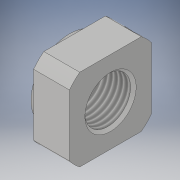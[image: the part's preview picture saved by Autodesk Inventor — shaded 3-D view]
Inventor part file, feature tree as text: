
AUTODESK INVENTOR PART (.ipt)
format: ipt  version: 2019 (Build 230136000, 136)  size: 162,304 bytes
history: native  units: mm
features: other x7, sketch x4, revolve x3, thread x2, extrude x1
ambient origin geometry x8: Origin, YZ Plane, XZ Plane, XY Plane, X Axis, Y Axis, Z Axis, Center Point
bodies: Solid1 (feature_tree)
feature tree (17):
  extrude  "Extrusion1"  TaperAngle=360.0deg  [1 undecoded]
  revolve  "Revolution1"  [1 undecoded]
  revolve  "Revolution2"  [1 undecoded]
  thread  "Thread1"  [1 undecoded]
  revolve  "Revolution3"  [1 undecoded]
  thread  "Thread2"  [1 undecoded]
  other  "to_collar_XY"
  other  "to_collar_YZ"
  other  "to_collar_ZX"
  other  "to_collar_X"
  other  "to_collar_Y"
  other  "to_collar_Z"
  other  "to_collar_Center"
  sketch  "Sketch_1"  dims[d0=7.0mm d1=0.0mm d2=360.0deg]
  sketch  "Sketch_2"  dims[d3=360.0deg d4=6.917mm d5=0.0mm]
  sketch  "Sketch_3"  dims[d6=360.0deg d7=5.7295mm d8=0.0mm d9=0.0mm]
  sketch  "Sketch_4"
note: 6 required parameter values undecoded (feature->parameter linkage not recoverable at this tier; creation-order binding heuristic only, values carry confidence <= 0.55)